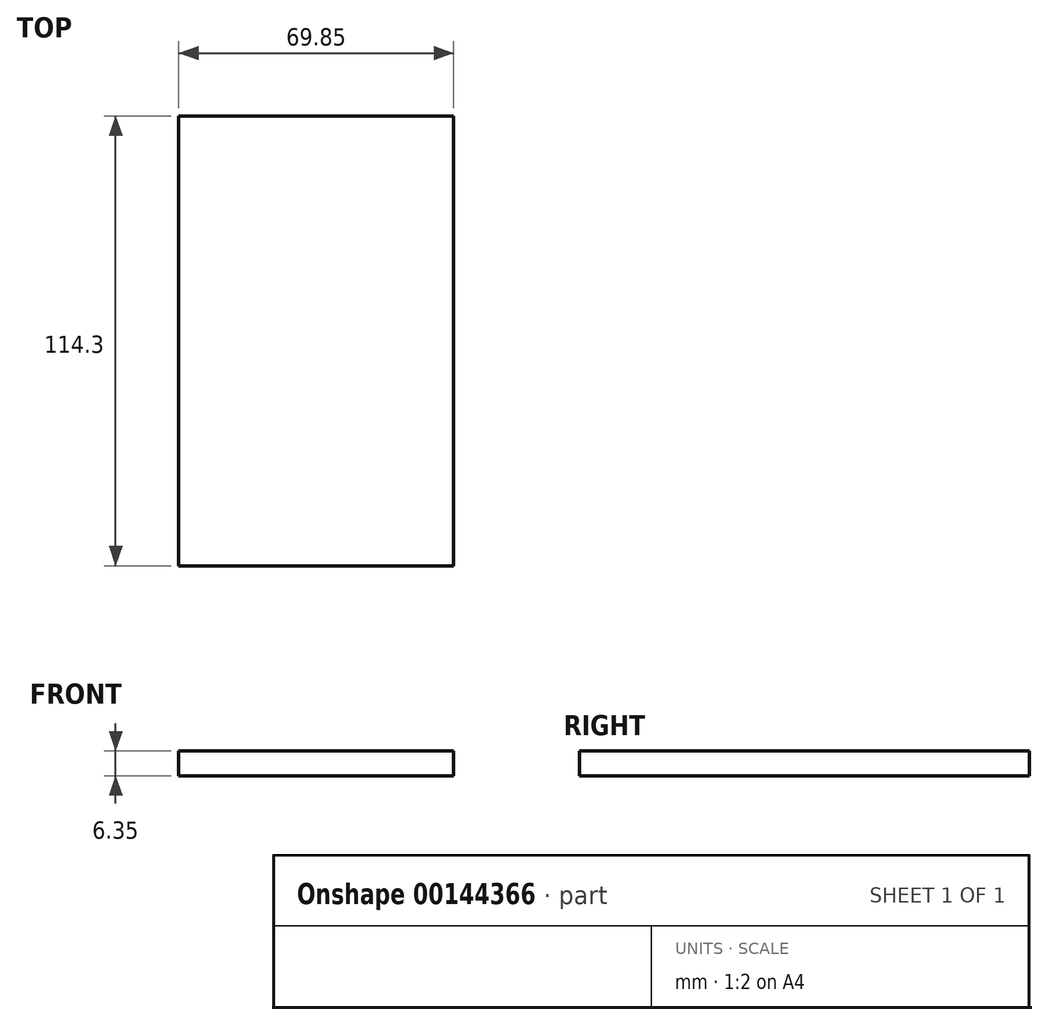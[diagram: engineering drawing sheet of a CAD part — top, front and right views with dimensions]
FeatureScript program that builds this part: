
annotation { "Feature Type Name" : "Feature", "Feature Type Description" : "" }
export const myFeature = defineFeature(function(context is Context, id is Id, definition is map)
    precondition{}
    {
        {
            var Q0;
            Q0=qCreatedBy(makeId("Top.planeOp"),FACE);
            var sketch = newSketch(context, id + "F0", { "sketchPlane" : qUnion([Q0])});
            skLineSegment(sketch, "E0.bottom", {"start": v(0, 0) * mm, "end": v(69.85, 0) * mm});
            skLineSegment(sketch, "E0.top", {"start": v(0, 114.3) * mm, "end": v(69.85, 114.3) * mm});
            skLineSegment(sketch, "E0.left", {"start": v(0, 0) * mm, "end": v(0, 114.3) * mm});
            skLineSegment(sketch, "E0.right", {"start": v(69.85, 0) * mm, "end": v(69.85, 114.3) * mm});
            skSolve(sketch);
        }
        {
            var Q0;
            Q0 = qSketchRegion(id + "F0", true);
            extrude(context, id + "F1", {"entities" : qUnion([Q0]), "depth" : 6.35 * mm});
        }
    });
